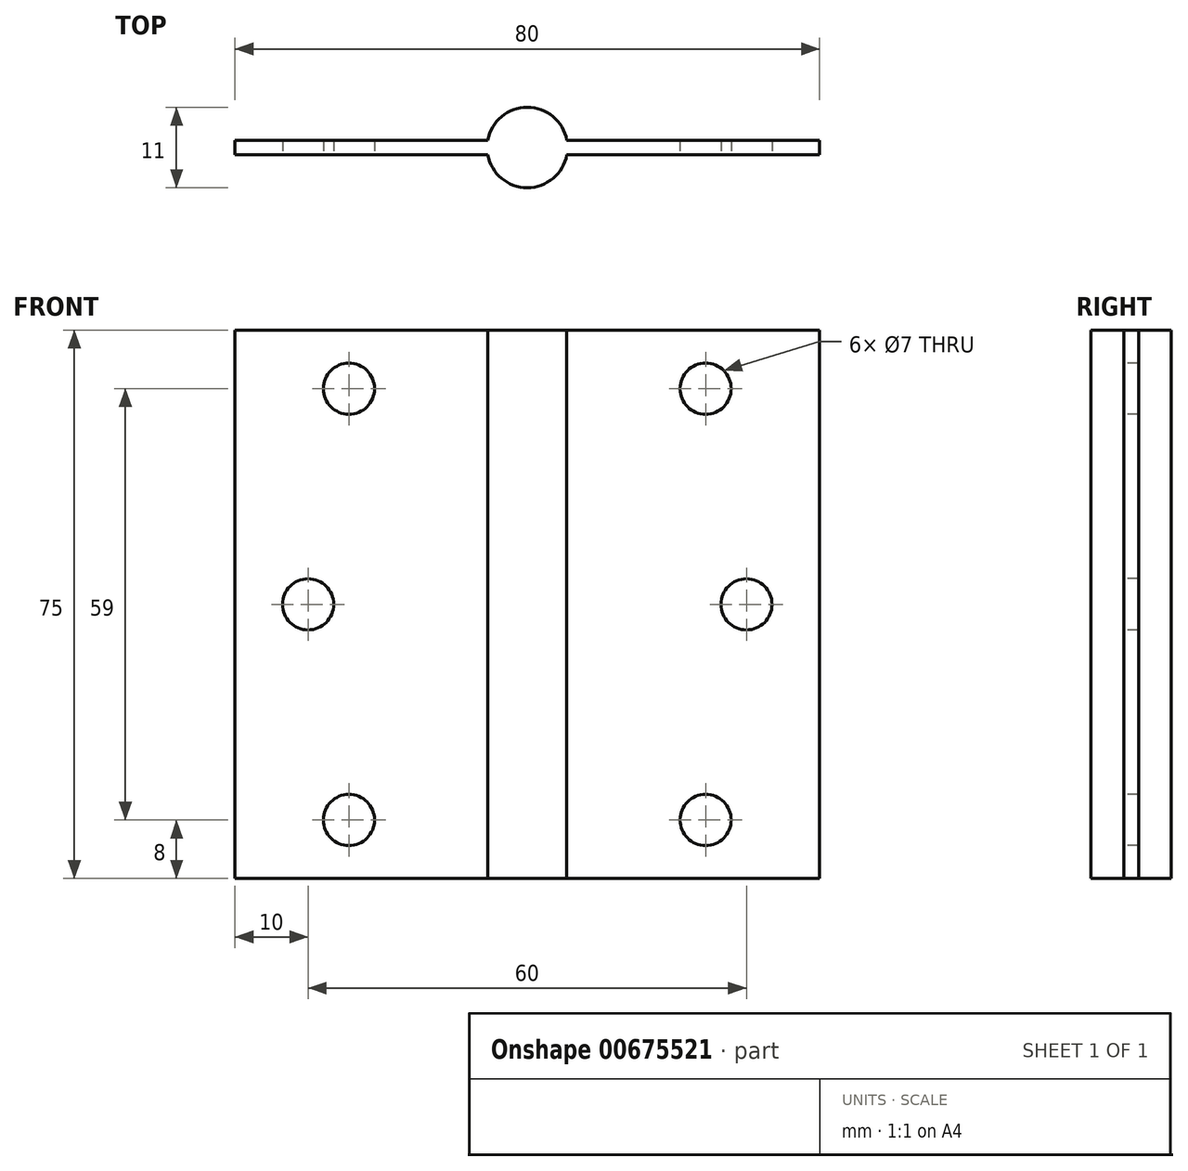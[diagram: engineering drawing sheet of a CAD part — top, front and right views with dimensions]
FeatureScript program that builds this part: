
annotation { "Feature Type Name" : "Feature", "Feature Type Description" : "" }
export const myFeature = defineFeature(function(context is Context, id is Id, definition is map)
    precondition{}
    {
        {
            var Q0;
            Q0=qCreatedBy(makeId("Front.planeOp"),FACE);
            var sketch = newSketch(context, id + "F0", { "sketchPlane" : qUnion([Q0])});
            skLineSegment(sketch, "E0.bottom", {"start": v(-17.5, 37.5) * mm, "end": v(17.5, 37.5) * mm});
            skLineSegment(sketch, "E0.top", {"start": v(-17.5, -37.5) * mm, "end": v(17.5, -37.5) * mm});
            skLineSegment(sketch, "E0.left", {"start": v(-17.5, 37.5) * mm, "end": v(-17.5, -37.5) * mm});
            skLineSegment(sketch, "E0.right", {"start": v(17.5, 37.5) * mm, "end": v(17.5, -37.5) * mm});
            skSolve(sketch);
        }
        {
            var Q0;
            Q0 = qSketchRegion(id + "F0", true);
            extrude(context, id + "F1", {"entities" : qUnion([Q0]), "depth" : 2 * mm, "offsetDistance" : 25 * mm});
        }
        {
            var Q0;
            Q0=makeQuery(id+"F1.opExtrude","SWEPT_FACE",FACE,{"disambiguationData":[OSD([sQuery(id+"F0.wireOp",EDGE,"E0.bottom")])]});
            var sketch = newSketch(context, id + "F2", { "sketchPlane" : qUnion([Q0])});
            skLineSegment(sketch, "E1", {"start": v(-17.5, -1) * mm, "end": v(-22.5, -1) * mm, "construction": true});
            skCircle(sketch, "E2", {"center": v(-22.5, -1) * mm, "radius": 5.5 * mm});
            skSolve(sketch);
        }
        {
            var Q0;
            Q0 = qSketchRegion(id + "F2", true);
            extrude(context, id + "F3", {"entities" : qUnion([Q0]), "oppositeDirection" : true, "depth" : 75 * mm, "offsetDistance" : 25 * mm});
        }
        {
            var Q0;
            Q0=makeQuery(id+"F1.opExtrude","CAP_FACE",FACE,{"disambiguationData":[OSD([sQuery(id+"F0.wireOp",EDGE,"E0.bottom"),sQuery(id+"F0.wireOp",EDGE,"E0.top"),sQuery(id+"F0.wireOp",EDGE,"E0.left"),sQuery(id+"F0.wireOp",EDGE,"E0.right")])],"isStart":false});
            var sketch = newSketch(context, id + "F4", { "sketchPlane" : qUnion([Q0])});
            skLineSegment(sketch, "E3", {"start": v(-17.5, 37.5) * mm, "end": v(-27.5, 37.5) * mm, "construction": true});
            skLineSegment(sketch, "E4", {"start": v(-27.5, 37.5) * mm, "end": v(-27.5, -37.5) * mm});
            skLineSegment(sketch, "E5", {"start": v(-27.5, -37.5) * mm, "end": v(-62.5, -37.5) * mm});
            skLineSegment(sketch, "E6", {"start": v(-62.5, -37.5) * mm, "end": v(-62.5, 37.5) * mm});
            skLineSegment(sketch, "E7", {"start": v(-27.5, 37.5) * mm, "end": v(-62.5, 37.5) * mm});
            skSolve(sketch);
        }
        {
            var Q0;
            Q0 = qSketchRegion(id + "F4", true);
            extrude(context, id + "F5", {"entities" : qUnion([Q0]), "oppositeDirection" : true, "depth" : 2 * mm, "offsetDistance" : 25 * mm});
        }
        {
            var Q0;
            Q0=makeQuery(id+"F1.opExtrude","SWEPT_BODY",BODY,{"disambiguationData":[OSD([sQuery(id+"F0.wireOp",EDGE,"E0.bottom"),sQuery(id+"F0.wireOp",EDGE,"E0.top"),sQuery(id+"F0.wireOp",EDGE,"E0.left"),sQuery(id+"F0.wireOp",EDGE,"E0.right")])]});
            var Q1;
            Q1=makeQuery(id+"F3.opExtrude","SWEPT_BODY",BODY,{"disambiguationData":[OSD([sQuery(id+"F2.wireOp",EDGE,"E2")])]});
            var Q2;
            Q2=makeQuery(id+"F5.opExtrude","SWEPT_BODY",BODY,{"disambiguationData":[OSD([sQuery(id+"F4.wireOp",EDGE,"E4"),sQuery(id+"F4.wireOp",EDGE,"E5"),sQuery(id+"F4.wireOp",EDGE,"E6"),sQuery(id+"F4.wireOp",EDGE,"E7")])]});
            booleanBodies(context, id + "F6", {"operationType" : BooleanOperationType.UNION, "tools" : qUnion([Q0, Q1, Q2])});
        }
        {
            var Q0;
            Q0=makeQuery(id+"F1.opExtrude","CAP_FACE",FACE,{"disambiguationData":[OSD([sQuery(id+"F0.wireOp",EDGE,"E0.bottom"),sQuery(id+"F0.wireOp",EDGE,"E0.top"),sQuery(id+"F0.wireOp",EDGE,"E0.left"),sQuery(id+"F0.wireOp",EDGE,"E0.right")])],"isStart":false});
            var sketch = newSketch(context, id + "F7", { "sketchPlane" : qUnion([Q0])});
            skLineSegment(sketch, "E8", {"start": v(-17.1, -29.5) * mm, "end": v(1.9, -29.5) * mm, "construction": true});
            skCircle(sketch, "E9", {"center": v(1.9, -29.5) * mm, "radius": 3.5 * mm});
            skCircle(sketch, "E10.MirrorC", {"center": v(1.9, 29.5) * mm, "radius": 3.5 * mm});
            skLineSegment(sketch, "E11", {"start": v(17.5, 0) * mm, "end": v(7.5, 0) * mm, "construction": true});
            skCircle(sketch, "E12", {"center": v(7.5, 0) * mm, "radius": 3.5 * mm});
            skSolve(sketch);
        }
        {
            var Q0;
            Q0 = qSketchRegion(id + "F7", true);
            extrude(context, id + "F8", {"entities" : qUnion([Q0]), "operationType" : NewBodyOperationType.REMOVE, "endBound" : BoundingType.THROUGH_ALL, "oppositeDirection" : true, "depth" : 25 * mm, "offsetDistance" : 25 * mm});
        }
        {
            var Q0;
            Q0=makeQuery(id+"F5.opExtrude","CAP_FACE",FACE,{"disambiguationData":[OSD([sQuery(id+"F4.wireOp",EDGE,"E4"),sQuery(id+"F4.wireOp",EDGE,"E5"),sQuery(id+"F4.wireOp",EDGE,"E6"),sQuery(id+"F4.wireOp",EDGE,"E7")])],"isStart":true});
            var sketch = newSketch(context, id + "F9", { "sketchPlane" : qUnion([Q0])});
            skLineSegment(sketch, "E13", {"start": v(-27.9, -29.5) * mm, "end": v(-46.9, -29.5) * mm, "construction": true});
            skCircle(sketch, "E14", {"center": v(-46.9, -29.5) * mm, "radius": 3.5 * mm});
            skCircle(sketch, "E15.MirrorC", {"center": v(-46.9, 29.5) * mm, "radius": 3.5 * mm});
            skLineSegment(sketch, "E16", {"start": v(-62.5, 0) * mm, "end": v(-52.5, 0) * mm, "construction": true});
            skCircle(sketch, "E17", {"center": v(-52.5, 0) * mm, "radius": 3.5 * mm});
            skSolve(sketch);
        }
        {
            var Q0;
            Q0 = qSketchRegion(id + "F9", true);
            extrude(context, id + "F10", {"entities" : qUnion([Q0]), "operationType" : NewBodyOperationType.REMOVE, "endBound" : BoundingType.THROUGH_ALL, "oppositeDirection" : true, "depth" : 25 * mm, "offsetDistance" : 25 * mm});
        }
    });
